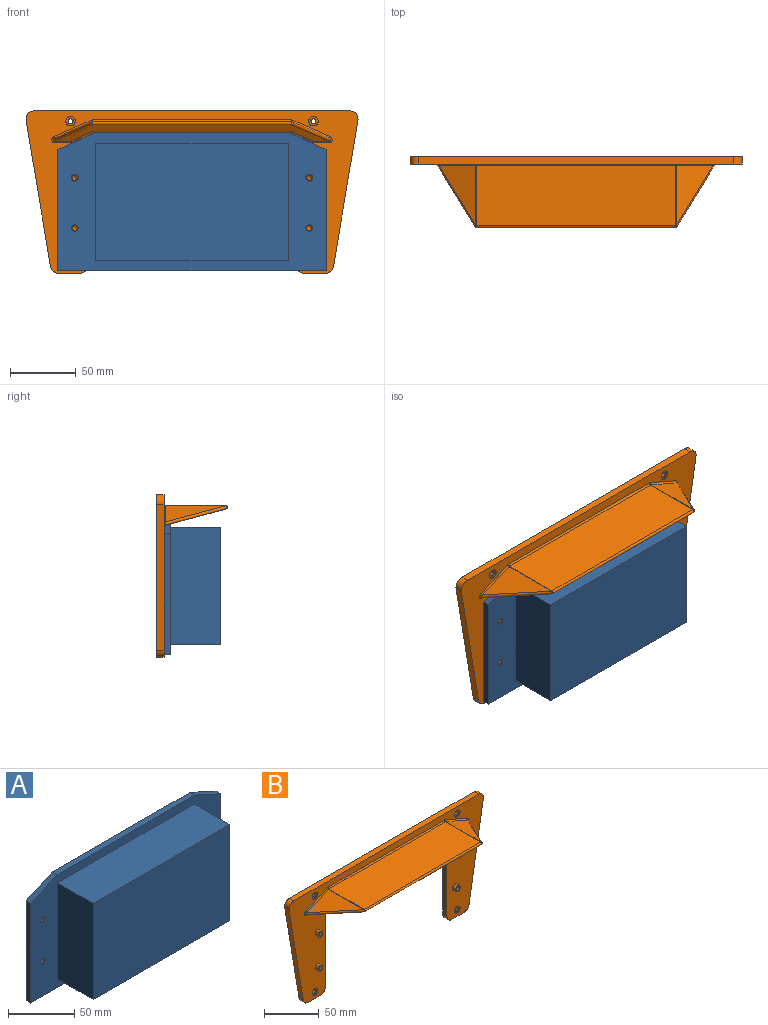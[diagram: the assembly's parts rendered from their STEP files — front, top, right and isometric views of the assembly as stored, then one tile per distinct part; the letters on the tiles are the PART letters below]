
ASSEMBLY  parts=2 mates=1
PART A: 30 faces, bbox 203.2x43.2x104.8 mm
  f0: plane 203.2x104.77mm, normal (0,-1,0), area 7867.9mm2, adj f1,f2,f3,f4,f5,f6,f8,f9
  f1: plane 27.94x12.7mm, normal (-0.41,0,0.91), area 155.9mm2, adj f0,f2,f6,f7
  f2: plane 92.07x5.08mm, normal (-1,0,0), area 467.7mm2, adj f0,f1,f3,f7
  f3: plane 203.2x5.08mm, normal (0,0,-1), area 1032.3mm2, adj f0,f2,f4,f7
  f4: plane 92.07x5.08mm, normal (1,0,0), area 467.7mm2, adj f0,f3,f5,f7
  f5: plane 27.94x12.7mm, normal (0.41,0,0.91), area 155.9mm2, adj f0,f4,f6,f7
  f6: plane 147.32x5.08mm, normal (0,0,1), area 748.4mm2, adj f0,f1,f5,f7
  f7: plane 203.2x104.77mm, normal (0,1,0), area 10090.2mm2, adj f1,f2,f3,f4,f5,f6,f13,f14
  f8: plane 146.05x38.1mm, normal (0,0,1), area 5564.5mm2, adj f0,f9,f11,f12
  f9: plane 88.9x38.1mm, normal (-1,0,0), area 3387.1mm2, adj f0,f8,f10,f12
  f10: plane 146.05x38.1mm, normal (0,0,-1), area 5564.5mm2, adj f0,f9,f11,f12
  f11: plane 88.9x38.1mm, normal (1,0,0), area 3387.1mm2, adj f0,f8,f10,f12
  f12: plane 146.05x88.9mm, normal (0,-1,0), area 12983.8mm2, adj f8,f9,f10,f11
  f13: plane 135.89x38.1mm, normal (0,0,-1), area 5177.4mm2, adj f7,f14,f16,f17
  f14: plane 78.74x38.1mm, normal (1,0,0), area 3000mm2, adj f7,f13,f15,f17
  f15: plane 135.89x38.1mm, normal (0,0,1), area 5177.4mm2, adj f7,f14,f16,f17
  f16: plane 78.74x38.1mm, normal (-1,0,0), area 3000mm2, adj f7,f13,f15,f17
  f17: plane 135.89x78.74mm, normal (0,1,0), area 10700mm2, adj f13,f14,f15,f16
  f18: cylinder r=3.38mm len=6.76mm, axis (0,1,0), area 86.3mm2, adj f7,f19
  f19: plane 6.76x6.76mm, normal (0,1,0), area 15.4mm2, adj f18,f28
  f20: cylinder r=3.38mm len=6.76mm, axis (0,1,0), area 86.3mm2, adj f7,f21
  f21: plane 6.76x6.76mm, normal (0,1,0), area 15.4mm2, adj f20,f27
  f22: cylinder r=3.38mm len=6.76mm, axis (0,1,0), area 86.3mm2, adj f7,f23
  f23: plane 6.76x6.76mm, normal (0,1,0), area 15.4mm2, adj f22,f29
  f24: cylinder r=3.38mm len=6.76mm, axis (0,1,0), area 86.3mm2, adj f7,f25
  f25: plane 6.76x6.76mm, normal (0,1,0), area 15.4mm2, adj f24,f26
  f26: cylinder r=2.55mm len=5.11mm, axis (0,1,0), area 16.3mm2, adj f0,f25
  f27: cylinder r=2.55mm len=5.11mm, axis (0,1,0), area 16.3mm2, adj f0,f21
  f28: cylinder r=2.55mm len=5.11mm, axis (0,1,0), area 16.3mm2, adj f0,f19
  f29: cylinder r=2.55mm len=5.11mm, axis (0,1,0), area 16.3mm2, adj f0,f23
PART B: 83 faces, bbox 251.7x53.8x123.2 mm
  f0: plane 207.45x46.24mm, normal (0,-0.26,-0.97), area 3446mm2, adj f27,f30,f31,f34,f35,f38,f43,f44
  f1: plane 45.57x27.82mm, normal (0.4,0,0.92), area 692.3mm2, adj f48,f51,f54
  f2: plane 28.18x17.21mm, normal (-0.4,0,-0.92), area 264.8mm2, adj f33,f42,f43
  f3: plane 148.06x28.98mm, normal (0,0,-1), area 4290.5mm2, adj f26,f32,f33,f34
  f4: plane 150.99x45.57mm, normal (0,0,1), area 6880.2mm2, adj f40,f44,f48,f49
  f5: plane 251.7x123.19mm, normal (0,-1,0), area 9666.4mm2, adj f6,f7,f8,f9,f11,f12,f13,f15
  f6: plane 239x5.72mm, normal (0,0,1), area 1365.9mm2, adj f5,f14,f15,f22
  f7: plane 110.49x18.47mm, normal (-0.99,0,-0.16), area 640.2mm2, adj f5,f14,f15,f16
  f8: plane 16.05x5.72mm, normal (0,0,-1), area 91.7mm2, adj f5,f14,f16,f17
  f9: plane 93.98x5.72mm, normal (1,0,0), area 537.1mm2, adj f5,f14,f17,f18
  f10: plane 144.58x5.72mm, normal (0,0,-1), area 826.3mm2, adj f14,f18,f19,f32
  f11: plane 93.98x5.72mm, normal (-1,0,0), area 537.1mm2, adj f5,f14,f19,f20
  f12: plane 16.05x5.72mm, normal (0,0,-1), area 91.7mm2, adj f5,f14,f20,f21
  f13: plane 110.49x18.47mm, normal (0.99,0,-0.16), area 640.2mm2, adj f5,f14,f21,f22
  f14: plane 251.7x123.19mm, normal (0,1,0), area 11893.3mm2, adj f6,f7,f8,f9,f10,f11,f12,f13
  f15: cylinder r=6.35mm len=7.4mm, axis (0,-1,0), area 63mm2, adj f5,f6,f7,f14
  f16: cylinder r=6.35mm len=6.26mm, axis (0,1,0), area 51mm2, adj f5,f7,f8,f14
  f17: cylinder r=6.35mm len=6.35mm, axis (0,-1,0), area 57mm2, adj f5,f8,f9,f14
  f18: cylinder r=6.35mm len=6.35mm, axis (0,1,0), area 57mm2, adj f5,f9,f10,f14
  f19: cylinder r=6.35mm len=6.35mm, axis (0,-1,0), area 57mm2, adj f5,f10,f11,f14
  f20: cylinder r=6.35mm len=6.35mm, axis (0,-1,0), area 57mm2, adj f5,f11,f12,f14
  f21: cylinder r=6.35mm len=6.26mm, axis (0,1,0), area 51mm2, adj f5,f12,f13,f14
  f22: cylinder r=6.35mm len=7.4mm, axis (0,1,0), area 63mm2, adj f5,f6,f13,f14
  f23: plane 28.18x17.21mm, normal (0.4,0,-0.92), area 264.8mm2, adj f25,f26,f27
  f24: plane 45.57x27.82mm, normal (-0.4,0,0.92), area 692.3mm2, adj f35,f40,f41
  f25: cylinder r=1.27mm len=17.72mm, axis (0.92,0,0.4), area 37.5mm2, adj f5,f23,f28,f29
  f26: cylinder r=1.27mm len=28.98mm, axis (0,1,0), area 15.1mm2, adj f3,f23,f29,f30
  f27: cylinder r=1.27mm len=29.17mm, axis (-0.51,0.83,-0.22), area 21.1mm2, adj f0,f23,f28,f30
  f28: bspline ~2.13x1.73mm, area 2.1mm2, adj f5,f25,f27,f31
  f29: sphere r=1.27mm, area 0.7mm2, adj f25,f26,f32
  f30: bspline ~1.82x1.61mm, area 0.5mm2, adj f0,f26,f27,f34
  f31: cylinder r=1.27mm len=11.06mm, axis (1,0,0), area 18.4mm2, adj f0,f5,f28,f36
  f32: cylinder r=1.27mm len=148.06mm, axis (1,0,0), area 295.4mm2, adj f3,f5,f10,f29,f37
  f33: cylinder r=1.27mm len=28.98mm, axis (0,1,0), area 15.1mm2, adj f2,f3,f37,f38
  f34: cylinder r=1.27mm len=148.06mm, axis (-1,0,0), area 49.2mm2, adj f0,f3,f30,f38
  f35: cylinder r=1.27mm len=47.69mm, axis (-0.51,0.83,-0.22), area 188.8mm2, adj f0,f24,f36,f39
  f36: bspline ~4.96x2.57mm, area 8.3mm2, adj f5,f31,f35,f41
  f37: sphere r=1.27mm, area 0.7mm2, adj f32,f33,f42
  f38: bspline ~1.89x1.81mm, area 0.5mm2, adj f0,f33,f34,f43
  f39: sphere r=1.27mm, area 3.3mm2, adj f35,f40,f44
  f40: cylinder r=1.27mm len=45.57mm, axis (0,1,0), area 23.9mm2, adj f4,f24,f39,f45
  f41: cylinder r=1.27mm len=28.33mm, axis (-0.92,0,-0.4), area 60.6mm2, adj f5,f24,f36,f45
  f42: cylinder r=1.27mm len=17.72mm, axis (0.92,0,-0.4), area 37.5mm2, adj f2,f5,f37,f46
  f43: cylinder r=1.27mm len=29.17mm, axis (-0.51,-0.83,0.22), area 21.1mm2, adj f0,f2,f38,f46
  f44: cylinder r=1.27mm len=150.99mm, axis (1,0,0), area 552.2mm2, adj f0,f4,f39,f47
  f45: torus R=2.54mm, axis (0,-1,0), area 1.4mm2, adj f5,f40,f41,f49
  f46: bspline ~2.13x1.73mm, area 2.1mm2, adj f5,f42,f43,f50
  f47: sphere r=1.27mm, area 3.3mm2, adj f44,f48,f51
  f48: cylinder r=1.27mm len=45.57mm, axis (0,1,0), area 23.9mm2, adj f1,f4,f47,f52
  f49: cylinder r=1.27mm len=150.99mm, axis (-1,0,0), area 301.2mm2, adj f4,f5,f45,f52
  f50: cylinder r=1.27mm len=11.06mm, axis (1,0,0), area 18.4mm2, adj f0,f5,f46,f53
  f51: cylinder r=1.27mm len=47.69mm, axis (0.51,0.83,-0.22), area 188.8mm2, adj f0,f1,f47,f53
  f52: torus R=2.54mm, axis (0,-1,0), area 1.4mm2, adj f5,f48,f49,f54
  f53: bspline ~4.96x2.57mm, area 8.3mm2, adj f5,f50,f51,f54
  f54: cylinder r=1.27mm len=28.33mm, axis (-0.92,0,0.4), area 60.6mm2, adj f1,f5,f52,f53
  f55: cylinder r=1.9mm len=4.45mm, axis (0,-1,0), area 53mm2, adj f14,f56
  f56: plane 7.14x7.14mm, normal (0,-1,0), area 28.8mm2, adj f55,f57
  f57: cylinder r=3.57mm len=7.14mm, axis (0,-1,0), area 28.5mm2, adj f5,f56
  f58: cylinder r=1.9mm len=4.45mm, axis (0,-1,0), area 53mm2, adj f14,f59
  f59: plane 7.14x7.14mm, normal (0,-1,0), area 28.8mm2, adj f58,f60
  f60: cylinder r=3.57mm len=7.14mm, axis (0,-1,0), area 28.5mm2, adj f5,f59
  f61: cylinder r=1.9mm len=4.45mm, axis (0,-1,0), area 53mm2, adj f14,f62
  f62: plane 7.14x7.14mm, normal (0,-1,0), area 28.8mm2, adj f61,f63
  f63: cylinder r=3.57mm len=7.14mm, axis (0,-1,0), area 28.5mm2, adj f5,f62
  f64: cylinder r=1.9mm len=4.45mm, axis (0,-1,0), area 53mm2, adj f14,f65
  f65: plane 7.14x7.14mm, normal (0,-1,0), area 28.8mm2, adj f64,f66
  f66: cylinder r=3.57mm len=7.14mm, axis (0,-1,0), area 28.5mm2, adj f5,f65
  f67: cylinder r=3.17mm len=6.35mm, axis (0,1,0), area 76mm2, adj f5,f68
  f68: plane 6.35x6.35mm, normal (0,-1,0), area 20.3mm2, adj f67,f82
  f69: cylinder r=3.17mm len=6.35mm, axis (0,1,0), area 76mm2, adj f5,f70
  f70: plane 6.35x6.35mm, normal (0,-1,0), area 20.3mm2, adj f69,f80
  f71: cylinder r=3.17mm len=6.35mm, axis (0,1,0), area 76mm2, adj f5,f72
  f72: plane 6.35x6.35mm, normal (0,-1,0), area 20.3mm2, adj f71,f78
  f73: cylinder r=3.17mm len=6.35mm, axis (0,1,0), area 76mm2, adj f5,f74
  f74: plane 6.35x6.35mm, normal (0,-1,0), area 20.3mm2, adj f73,f76
  f75: cone r=0mm half-angle=59deg, axis (0,-1,0), area 13.2mm2, adj f76
  f76: cylinder r=1.9mm len=6.99mm, axis (0,-1,0), area 83.3mm2, adj f74,f75
  f77: cone r=0mm half-angle=59deg, axis (0,-1,0), area 13.2mm2, adj f78
  f78: cylinder r=1.9mm len=6.99mm, axis (0,-1,0), area 83.3mm2, adj f72,f77
  f79: cone r=0mm half-angle=59deg, axis (0,-1,0), area 13.2mm2, adj f80
  f80: cylinder r=1.9mm len=6.99mm, axis (0,-1,0), area 83.3mm2, adj f70,f79
  f81: cone r=0mm half-angle=59deg, axis (0,-1,0), area 13.2mm2, adj f82
  f82: cylinder r=1.9mm len=6.99mm, axis (0,-1,0), area 83.3mm2, adj f68,f81
PLACE A t=(-54.73,-101.59,-141.02)mm
PLACE B t=(-54.73,-96.13,-89.25)mm
MATE planar A.f24 <-> B.f71  axis (0,1,0) through (34.17,-105.65,-122.8)mm
